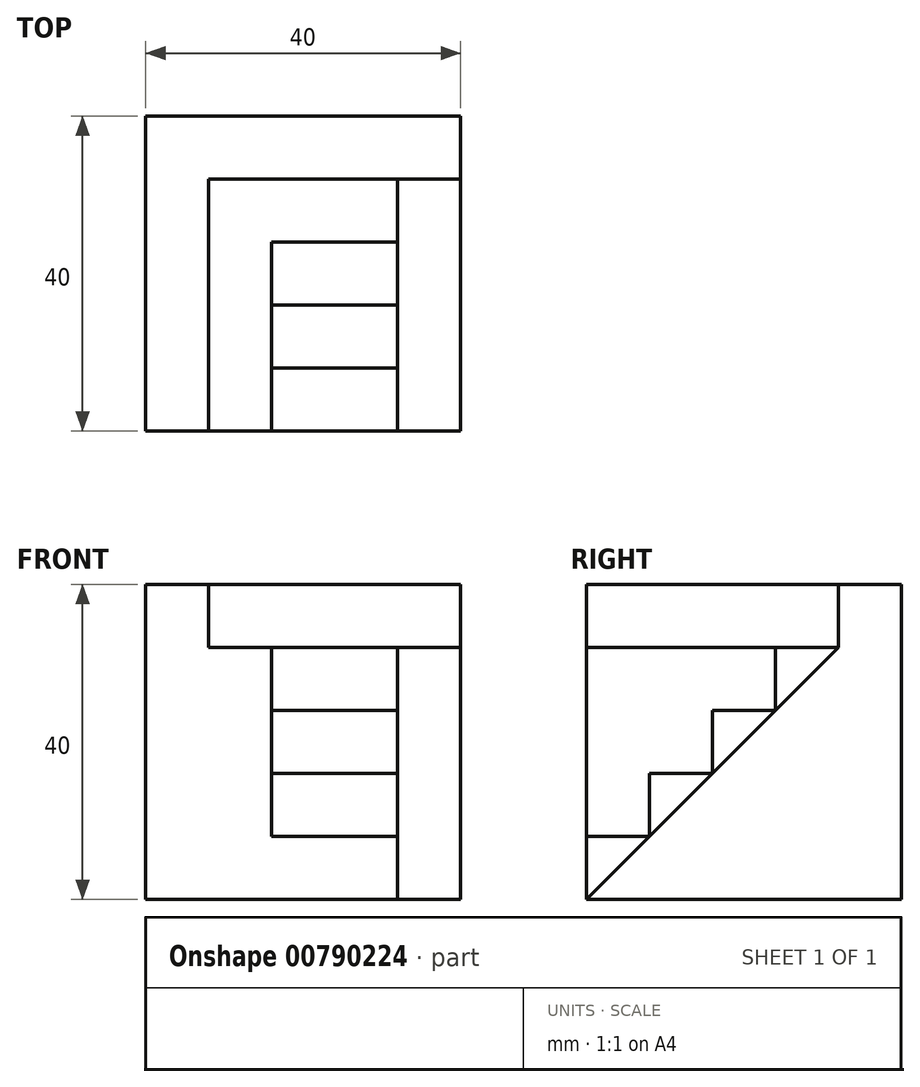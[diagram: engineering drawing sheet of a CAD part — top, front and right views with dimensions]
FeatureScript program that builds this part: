
annotation { "Feature Type Name" : "Feature", "Feature Type Description" : "" }
export const myFeature = defineFeature(function(context is Context, id is Id, definition is map)
    precondition{}
    {
        {
            var Q0;
            Q0=qCreatedBy(makeId("Top.planeOp"),FACE);
            var sketch = newSketch(context, id + "F0", { "sketchPlane" : qUnion([Q0])});
            skLineSegment(sketch, "E0.bottom", {"start": v(-20, 20) * mm, "end": v(20, 20) * mm});
            skLineSegment(sketch, "E0.top", {"start": v(-20, -20) * mm, "end": v(20, -20) * mm});
            skLineSegment(sketch, "E0.left", {"start": v(-20, 20) * mm, "end": v(-20, -20) * mm});
            skLineSegment(sketch, "E0.right", {"start": v(20, 20) * mm, "end": v(20, 12) * mm});
            skPoint(sketch, "E0.middle", {"position": v(0, 0) * mm});
            skLineSegment(sketch, "E1", {"start": v(-20, 20) * mm, "end": v(-12, 20) * mm});
            skLineSegment(sketch, "E2", {"start": v(-12, 12) * mm, "end": v(-12, -20) * mm});
            skLineSegment(sketch, "E3", {"start": v(-12, 12) * mm, "end": v(20, 12) * mm});
            skPoint(sketch, "E4.startSnap0", {"position": v(-20, 0) * mm});
            skPoint(sketch, "E5.orphan", {"position": v(20, 0) * mm});
            skPoint(sketch, "E4.start.orphan", {"position": v(-12, 0) * mm});
            skLineSegment(sketch, "E6", {"start": v(20, 12) * mm, "end": v(20, -20) * mm});
            skLineSegment(sketch, "E7", {"start": v(12, 12) * mm, "end": v(12, -20) * mm});
            skLineSegment(sketch, "E8", {"start": v(-4, -12) * mm, "end": v(12, -12) * mm});
            skLineSegment(sketch, "E9", {"start": v(-4, -4) * mm, "end": v(12, -4) * mm});
            skLineSegment(sketch, "E10", {"start": v(-4, 4) * mm, "end": v(12, 4) * mm});
            skPoint(sketch, "E11.orphan", {"position": v(20, 4) * mm});
            skPoint(sketch, "E12.orphan", {"position": v(20, -4) * mm});
            skPoint(sketch, "E13.orphan", {"position": v(20, -12) * mm});
            skLineSegment(sketch, "E14", {"start": v(-4, 4) * mm, "end": v(-4, -20) * mm});
            skSolve(sketch);
        }
        {
            var Q0;
            {var subQ4=sQuery(id+"F0.wireOp",EDGE,"E6");Q0=makeQuery(id+"F0.imprint","IMPRINT",FACE,{"disambiguationData":[TD([[makeQuery(id+"F0.imprint","IMPRINT",EDGE,{"derivedFrom":subQ4}),-1.0]])]});}
            extrude(context, id + "F1", {"entities" : qUnion([Q0]), "depth" : 32 * mm, "offsetDistance" : 25 * mm});
        }
        {
            var Q0;
            Q0=makeQuery(id+"F1.opExtrude","SWEPT_FACE",FACE,{"disambiguationData":[OSD([sQuery(id+"F0.wireOp",EDGE,"E6")])]});
            var sketch = newSketch(context, id + "F2", { "sketchPlane" : qUnion([Q0])});
            skLineSegment(sketch, "E15", {"start": v(12, 32) * mm, "end": v(-20, 0) * mm});
            skSolve(sketch);
        }
        {
            var Q0;
            Q0=makeQuery(id+"F2.imprint","IMPRINT",FACE,{"disambiguationData":[TD([[makeQuery(id+"F2.imprint","IMPRINT",EDGE,{"derivedFrom":sQuery(id+"F2.wireOp",EDGE,"E15")}),-1.0]])]});
            extrude(context, id + "F3", {"entities" : qUnion([Q0]), "operationType" : NewBodyOperationType.REMOVE, "oppositeDirection" : true, "depth" : 25 * mm, "offsetDistance" : 25 * mm});
        }
        {
            var Q0;
            Q0=makeQuery(id+"F0.imprint","IMPRINT",FACE,{"disambiguationData":[TD([[makeQuery(id+"F0.imprint","IMPRINT",EDGE,{"derivedFrom":sQuery(id+"F0.wireOp",EDGE,"E0.bottom")}),-1.0]])]});
            extrude(context, id + "F4", {"entities" : qUnion([Q0]), "operationType" : NewBodyOperationType.ADD, "depth" : 40 * mm, "offsetDistance" : 25 * mm});
        }
        {
            var Q0;
            {var subQ1=sQuery(id+"F0.wireOp",EDGE,"E2");Q0=makeQuery(id+"F0.imprint","IMPRINT",FACE,{"disambiguationData":[TD([[makeQuery(id+"F0.imprint","IMPRINT",EDGE,{"derivedFrom":subQ1}),1.0]])]});}
            extrude(context, id + "F5", {"entities" : qUnion([Q0]), "operationType" : NewBodyOperationType.ADD, "depth" : 32 * mm, "offsetDistance" : 25 * mm});
        }
        {
            var Q0;
            {var subQ0=sQuery(id+"F0.wireOp",EDGE,"E8");Q0=makeQuery(id+"F0.imprint","IMPRINT",FACE,{"disambiguationData":[TD([[makeQuery(id+"F0.imprint","IMPRINT",EDGE,{"derivedFrom":subQ0}),1.0]])]});}
            extrude(context, id + "F6", {"entities" : qUnion([Q0]), "operationType" : NewBodyOperationType.ADD, "depth" : 16 * mm, "offsetDistance" : 25 * mm});
        }
        {
            var Q0;
            {var subQ5=sQuery(id+"F0.wireOp",EDGE,"E8");Q0=makeQuery(id+"F0.imprint","IMPRINT",FACE,{"disambiguationData":[TD([[makeQuery(id+"F0.imprint","IMPRINT",EDGE,{"derivedFrom":subQ5}),-1.0]])]});}
            extrude(context, id + "F7", {"entities" : qUnion([Q0]), "operationType" : NewBodyOperationType.ADD, "depth" : 8 * mm, "offsetDistance" : 25 * mm});
        }
        {
            var Q0;
            {var subQ0=sQuery(id+"F0.wireOp",EDGE,"E9");Q0=makeQuery(id+"F0.imprint","IMPRINT",FACE,{"disambiguationData":[TD([[makeQuery(id+"F0.imprint","IMPRINT",EDGE,{"derivedFrom":subQ0}),1.0]])]});}
            extrude(context, id + "F8", {"entities" : qUnion([Q0]), "operationType" : NewBodyOperationType.ADD, "depth" : 24 * mm, "offsetDistance" : 25 * mm});
        }
    });
